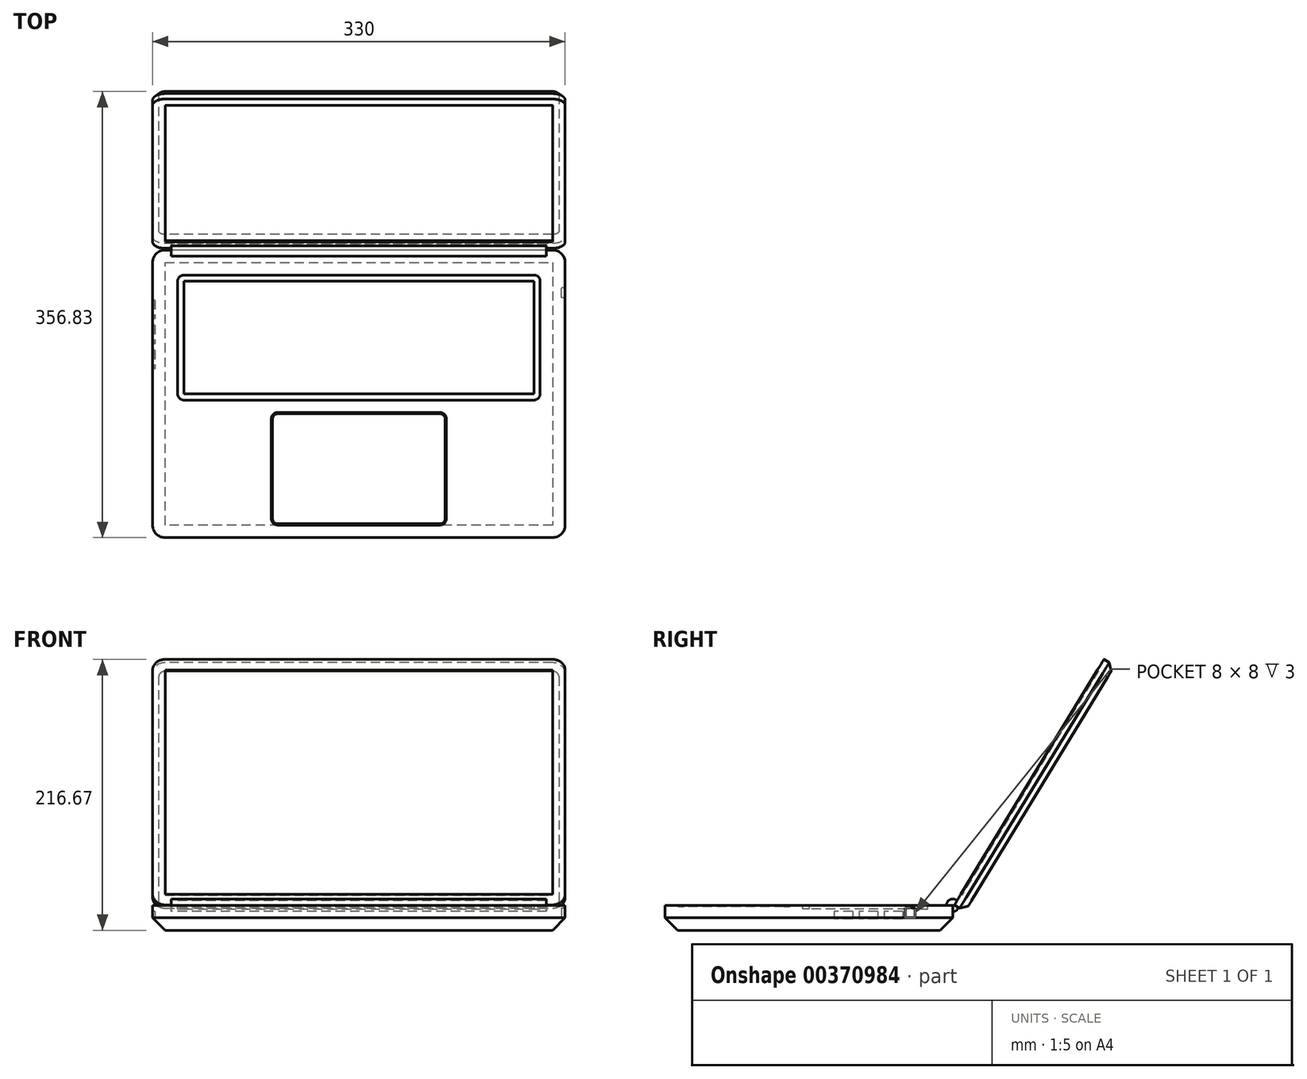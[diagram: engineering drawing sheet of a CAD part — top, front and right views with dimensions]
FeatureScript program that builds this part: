
annotation { "Feature Type Name" : "Feature", "Feature Type Description" : "" }
export const myFeature = defineFeature(function(context is Context, id is Id, definition is map)
    precondition{}
    {
        {
            var Q0;
            Q0=qCreatedBy(makeId("Right.planeOp"),FACE);
            var sketch = newSketch(context, id + "F0", { "sketchPlane" : qUnion([Q0])});
            skCircle(sketch, "E0", {"center": v(0, 0) * mm, "radius": 5 * mm});
            skSolve(sketch);
        }
        {
            var Q0;
            Q0=qCreatedBy(makeId("Right.planeOp"),FACE);
            var sketch = newSketch(context, id + "F1", { "sketchPlane" : qUnion([Q0])});
            skLineSegment(sketch, "E1.bottom", {"start": v(0, 0) * mm, "end": v(-230, 0) * mm});
            skLineSegment(sketch, "E1.top", {"start": v(0, -20) * mm, "end": v(-230, -20) * mm});
            skLineSegment(sketch, "E1.left", {"start": v(0, 0) * mm, "end": v(0, -20) * mm});
            skLineSegment(sketch, "E1.right", {"start": v(-230, 0) * mm, "end": v(-230, -20) * mm});
            skSolve(sketch);
        }
        {
            var Q0;
            Q0 = qSketchRegion(id + "F1", true);
            extrude(context, id + "F2", {"entities" : qUnion([Q0]), "endBound" : BoundingType.SYMMETRIC, "depth" : 330 * mm});
        }
        {
            var Q0;
            Q0 = qSketchRegion(id + "F0", true);
            extrude(context, id + "F3", {"entities" : qUnion([Q0]), "operationType" : NewBodyOperationType.ADD, "endBound" : BoundingType.SYMMETRIC, "depth" : 300 * mm});
        }
        {
            var Q0;
            Q0=makeQuery(id+"F2.opExtrude","CAP_EDGE",EDGE,{"disambiguationData":[OSD([sQuery(id+"F1.wireOp",EDGE,"V3VyQ788-CHpF-L9UI-HHIn-uLbdnDteFLPi")])],"isStart":false});
            var Q1;
            Q1=makeQuery(id+"F2.opExtrude","CAP_EDGE",EDGE,{"disambiguationData":[OSD([sQuery(id+"F1.wireOp",EDGE,"V3VyQ788-CHpF-L9UI-HHIn-uLbdnDteFLPi")])],"isStart":true});
            var Q2;
            Q2=makeQuery(id+"F2.opExtrude","CAP_EDGE",EDGE,{"disambiguationData":[OSD([sQuery(id+"F1.wireOp",EDGE,"1viRVT48-LFa6-ff3u-HfjB-U5OnZZm2wvsv")])],"isStart":false});
            var Q3;
            Q3=makeQuery(id+"F2.opExtrude","CAP_EDGE",EDGE,{"disambiguationData":[OSD([sQuery(id+"F1.wireOp",EDGE,"1viRVT48-LFa6-ff3u-HfjB-U5OnZZm2wvsv")])],"isStart":true});
            var Q4;
            Q4=makeQuery(id+"F2.opExtrude","CAP_EDGE",EDGE,{"disambiguationData":[OSD([sQuery(id+"F1.wireOp",EDGE,"E1.left")])],"isStart":true});
            var Q5;
            Q5=makeQuery(id+"F2.opExtrude","CAP_EDGE",EDGE,{"disambiguationData":[OSD([sQuery(id+"F1.wireOp",EDGE,"E1.right")])],"isStart":true});
            var Q6;
            Q6=makeQuery(id+"F2.opExtrude","CAP_EDGE",EDGE,{"disambiguationData":[OSD([sQuery(id+"F1.wireOp",EDGE,"E1.right")])],"isStart":false});
            var Q7;
            Q7=makeQuery(id+"F2.opExtrude","CAP_EDGE",EDGE,{"disambiguationData":[OSD([sQuery(id+"F1.wireOp",EDGE,"E1.left")])],"isStart":false});
            fillet(context, id + "F4", {"entities" : qUnion([Q0, Q1, Q2, Q3, Q4, Q5, Q6, Q7]), "radius" : 10 * mm, "tangentPropagation" : true, "allowEdgeOverflow" : false});
        }
        {
            var Q0;
            Q0=makeQuery(id+"F2.opExtrude","CAP_EDGE",EDGE,{"disambiguationData":[OSD([sQuery(id+"F1.wireOp",EDGE,"E1.top")])],"isStart":false});
            chamfer(context, id + "F5", {"entities" : qUnion([Q0]), "width" : 10 * mm, "tangentPropagation" : true});
        }
        {
            var Q0;
            Q0=makeQuery(id+"F2.opExtrude","SWEPT_FACE",FACE,{"disambiguationData":[OSD([sQuery(id+"F1.wireOp",EDGE,"E1.bottom")])]});
            var sketch = newSketch(context, id + "F6", { "sketchPlane" : qUnion([Q0])});
            skLineSegment(sketch, "E2.bottom", {"start": v(-140, -20) * mm, "end": v(140, -20) * mm});
            skLineSegment(sketch, "E2.top", {"start": v(-140, -120) * mm, "end": v(140, -120) * mm});
            skLineSegment(sketch, "E2.left", {"start": v(-145, -25) * mm, "end": v(-145, -115) * mm});
            skLineSegment(sketch, "E2.right", {"start": v(145, -25) * mm, "end": v(145, -115) * mm});
            skPoint(sketch, "E3.visualSharp", {"position": v(-145, -20) * mm});
            skArc(sketch, "E3.filletArc", {"start": v(-140, -20) * mm, "mid": v(-143.54, -21.46) * mm, "end": v(-145, -25) * mm});
            skPoint(sketch, "E4.visualSharp", {"position": v(-145, -120) * mm});
            skArc(sketch, "E4.filletArc", {"start": v(-145, -115) * mm, "mid": v(-143.54, -118.54) * mm, "end": v(-140, -120) * mm});
            skPoint(sketch, "E5.visualSharp", {"position": v(145, -120) * mm});
            skArc(sketch, "E5.filletArc", {"start": v(140, -120) * mm, "mid": v(143.54, -118.54) * mm, "end": v(145, -115) * mm});
            skPoint(sketch, "E6.visualSharp", {"position": v(145, -20) * mm});
            skArc(sketch, "E6.filletArc", {"start": v(145, -25) * mm, "mid": v(143.54, -21.46) * mm, "end": v(140, -20) * mm});
            skSolve(sketch);
        }
        {
            var Q0;
            Q0 = qSketchRegion(id + "F6", true);
            extrude(context, id + "F7", {"entities" : qUnion([Q0]), "operationType" : NewBodyOperationType.REMOVE, "oppositeDirection" : true, "depth" : 3 * mm});
        }
        {
            var Q0;
            Q0=makeQuery(id+"F7.boolean.opBoolean","COPY",FACE,{"derivedFrom":makeQuery(id+"F7.opExtrude","CAP_FACE",FACE,{"disambiguationData":[OSD([sQuery(id+"F6.wireOp",EDGE,"E2.bottom"),sQuery(id+"F6.wireOp",EDGE,"E2.top"),sQuery(id+"F6.wireOp",EDGE,"E2.left"),sQuery(id+"F6.wireOp",EDGE,"E2.right"),sQuery(id+"F6.wireOp",EDGE,"E3.filletArc"),sQuery(id+"F6.wireOp",EDGE,"E4.filletArc"),sQuery(id+"F6.wireOp",EDGE,"E5.filletArc"),sQuery(id+"F6.wireOp",EDGE,"E6.filletArc")])],"isStart":false})});
            var sketch = newSketch(context, id + "F8", { "sketchPlane" : qUnion([Q0])});
            skLineSegment(sketch, "E7.bottom", {"start": v(-140, -25) * mm, "end": v(140, -25) * mm});
            skLineSegment(sketch, "E7.top", {"start": v(-140, -115) * mm, "end": v(140, -115) * mm});
            skLineSegment(sketch, "E7.left", {"start": v(-140, -25) * mm, "end": v(-140, -115) * mm});
            skLineSegment(sketch, "E7.right", {"start": v(140, -25) * mm, "end": v(140, -115) * mm});
            skSolve(sketch);
        }
        {
            var Q0;
            Q0 = qSketchRegion(id + "F8", true);
            extrude(context, id + "F9", {"entities" : qUnion([Q0]), "operationType" : NewBodyOperationType.ADD, "depth" : 3 * mm});
        }
        {
            var Q0;
            Q0=makeQuery(id+"F2.opExtrude","SWEPT_FACE",FACE,{"disambiguationData":[OSD([sQuery(id+"F1.wireOp",EDGE,"E1.bottom")])]});
            var sketch = newSketch(context, id + "F10", { "sketchPlane" : qUnion([Q0])});
            skLineSegment(sketch, "E8.bottom", {"start": v(-65, -130) * mm, "end": v(65, -130) * mm});
            skLineSegment(sketch, "E8.top", {"start": v(-65, -220) * mm, "end": v(65, -220) * mm});
            skLineSegment(sketch, "E8.left", {"start": v(-70, -135) * mm, "end": v(-70, -215) * mm});
            skLineSegment(sketch, "E8.right", {"start": v(70, -135) * mm, "end": v(70, -215) * mm});
            skPoint(sketch, "E9.visualSharp", {"position": v(-70, -130) * mm});
            skArc(sketch, "E9.filletArc", {"start": v(-65, -130) * mm, "mid": v(-68.54, -131.46) * mm, "end": v(-70, -135) * mm});
            skPoint(sketch, "E10.visualSharp", {"position": v(-70, -220) * mm});
            skArc(sketch, "E10.filletArc", {"start": v(-70, -215) * mm, "mid": v(-68.54, -218.54) * mm, "end": v(-65, -220) * mm});
            skPoint(sketch, "E11.visualSharp", {"position": v(70, -220) * mm});
            skArc(sketch, "E11.filletArc", {"start": v(65, -220) * mm, "mid": v(68.54, -218.54) * mm, "end": v(70, -215) * mm});
            skPoint(sketch, "E12.visualSharp", {"position": v(70, -130) * mm});
            skArc(sketch, "E12.filletArc", {"start": v(70, -135) * mm, "mid": v(68.54, -131.46) * mm, "end": v(65, -130) * mm});
            skLineSegment(sketch, "E13.0", {"start": v(-65, -131) * mm, "end": v(65, -131) * mm});
            skArc(sketch, "E13.1", {"start": v(69, -135) * mm, "mid": v(67.83, -132.17) * mm, "end": v(65, -131) * mm});
            skArc(sketch, "E13.2", {"start": v(-65, -131) * mm, "mid": v(-67.83, -132.17) * mm, "end": v(-69, -135) * mm});
            skLineSegment(sketch, "E13.3", {"start": v(69, -135) * mm, "end": v(69, -215) * mm});
            skLineSegment(sketch, "E13.4", {"start": v(-69, -135) * mm, "end": v(-69, -215) * mm});
            skArc(sketch, "E13.5", {"start": v(-69, -215) * mm, "mid": v(-67.83, -217.83) * mm, "end": v(-65, -219) * mm});
            skLineSegment(sketch, "E13.6", {"start": v(-65, -219) * mm, "end": v(65, -219) * mm});
            skArc(sketch, "E13.7", {"start": v(65, -219) * mm, "mid": v(67.83, -217.83) * mm, "end": v(69, -215) * mm});
            skSolve(sketch);
        }
        {
            var Q0;
            Q0 = qSketchRegion(id + "F10", true);
            extrude(context, id + "F11", {"entities" : qUnion([Q0]), "operationType" : NewBodyOperationType.REMOVE, "oppositeDirection" : true, "depth" : 1 * mm});
        }
        {
            var Q0;
            Q0=qCreatedBy(makeId("Right.planeOp"),FACE);
            var sketch = newSketch(context, id + "F12", { "sketchPlane" : qUnion([Q0])});
            skLineSegment(sketch, "E14", {"start": v(1.37, 0.32) * mm, "end": v(9.84, -5) * mm});
            skLineSegment(sketch, "E15", {"start": v(9.84, -5) * mm, "end": v(129.43, 191.47) * mm});
            skLineSegment(sketch, "E16", {"start": v(129.43, 191.47) * mm, "end": v(120.9, 196.67) * mm});
            skLineSegment(sketch, "E17", {"start": v(120.9, 196.67) * mm, "end": v(1.37, 0.32) * mm});
            skSolve(sketch);
        }
        {
            var Q0;
            Q0 = qSketchRegion(id + "F12", true);
            extrude(context, id + "F13", {"entities" : qUnion([Q0]), "operationType" : NewBodyOperationType.ADD, "endBound" : BoundingType.SYMMETRIC, "depth" : 330 * mm});
        }
        {
            var Q0;
            Q0=makeQuery(id+"F13.opExtrude","CAP_EDGE",EDGE,{"disambiguationData":[OSD([sQuery(id+"F12.wireOp",EDGE,"E16")])],"isStart":true});
            var Q1;
            Q1=makeQuery(id+"F13.opExtrude","CAP_EDGE",EDGE,{"disambiguationData":[OSD([sQuery(id+"F12.wireOp",EDGE,"E16")])],"isStart":false});
            var Q2;
            Q2=makeQuery(id+"F13.opExtrude","CAP_EDGE",EDGE,{"disambiguationData":[OSD([sQuery(id+"F12.wireOp",EDGE,"E14")])],"isStart":false});
            var Q3;
            Q3=makeQuery(id+"F13.opExtrude","CAP_EDGE",EDGE,{"disambiguationData":[OSD([sQuery(id+"F12.wireOp",EDGE,"E14")])],"isStart":true});
            fillet(context, id + "F14", {"entities" : qUnion([Q0, Q1, Q2, Q3]), "radius" : 10 * mm, "tangentPropagation" : true, "allowEdgeOverflow" : false});
        }
        {
            var Q0;
            Q0=makeQuery(id+"F13.opExtrude","CAP_EDGE",EDGE,{"disambiguationData":[OSD([sQuery(id+"F12.wireOp",EDGE,"E15")])],"isStart":false});
            chamfer(context, id + "F15", {"entities" : qUnion([Q0]), "width" : 5 * mm, "tangentPropagation" : true});
        }
        {
            var Q0;
            Q0=makeQuery(id+"F13.opExtrude","SWEPT_FACE",FACE,{"disambiguationData":[OSD([sQuery(id+"F12.wireOp",EDGE,"E17")])]});
            var sketch = newSketch(context, id + "F16", { "sketchPlane" : qUnion([Q0])});
            skLineSegment(sketch, "E18.bottom", {"start": v(-155, 220.85) * mm, "end": v(155, 220.85) * mm});
            skLineSegment(sketch, "E18.top", {"start": v(-155, 10.92) * mm, "end": v(155, 10.92) * mm});
            skLineSegment(sketch, "E18.left", {"start": v(-155, 220.85) * mm, "end": v(-155, 10.92) * mm});
            skLineSegment(sketch, "E18.right", {"start": v(155, 220.85) * mm, "end": v(155, 10.92) * mm});
            skSolve(sketch);
        }
        {
            var Q0;
            Q0 = qSketchRegion(id + "F16", true);
            extrude(context, id + "F17", {"entities" : qUnion([Q0]), "operationType" : NewBodyOperationType.REMOVE, "oppositeDirection" : true, "depth" : 1 * mm});
        }
        {
            var Q0;
            Q0=makeQuery(id+"F2.opExtrude","CAP_FACE",FACE,{"disambiguationData":[OSD([sQuery(id+"F1.wireOp",EDGE,"E1.bottom"),sQuery(id+"F1.wireOp",EDGE,"E1.top"),sQuery(id+"F1.wireOp",EDGE,"E1.left"),sQuery(id+"F1.wireOp",EDGE,"E1.right")])],"isStart":true});
            var sketch = newSketch(context, id + "F18", { "sketchPlane" : qUnion([Q0])});
            skLineSegment(sketch, "E19.bottom", {"start": v(80, -5) * mm, "end": v(95, -5) * mm});
            skLineSegment(sketch, "E19.top", {"start": v(80, -11) * mm, "end": v(95, -11) * mm});
            skLineSegment(sketch, "E19.left", {"start": v(80, -5) * mm, "end": v(80, -11) * mm});
            skLineSegment(sketch, "E19.right", {"start": v(95, -5) * mm, "end": v(95, -11) * mm});
            skLineSegment(sketch, "E20.1.0.0", {"start": v(60, -5) * mm, "end": v(60, -11) * mm});
            skLineSegment(sketch, "E20.1.0.1", {"start": v(60, -5) * mm, "end": v(75, -5) * mm});
            skLineSegment(sketch, "E20.1.0.2", {"start": v(75, -5) * mm, "end": v(75, -11) * mm});
            skLineSegment(sketch, "E20.1.0.3", {"start": v(60, -11) * mm, "end": v(75, -11) * mm});
            skLineSegment(sketch, "E20.2.0.0", {"start": v(40, -5) * mm, "end": v(40, -11) * mm});
            skLineSegment(sketch, "E20.2.0.1", {"start": v(40, -5) * mm, "end": v(55, -5) * mm});
            skLineSegment(sketch, "E20.2.0.2", {"start": v(55, -5) * mm, "end": v(55, -11) * mm});
            skLineSegment(sketch, "E20.2.0.3", {"start": v(40, -11) * mm, "end": v(55, -11) * mm});
            skLineSegment(sketch, "E20.direction1", {"start": v(80, -11) * mm, "end": v(60, -11) * mm, "construction": true});
            skSolve(sketch);
        }
        {
            var Q0;
            Q0 = qSketchRegion(id + "F18", true);
            extrude(context, id + "F19", {"entities" : qUnion([Q0]), "operationType" : NewBodyOperationType.REMOVE, "oppositeDirection" : true, "depth" : 2 * mm});
        }
        {
            var Q0;
            Q0=makeQuery(id+"F2.opExtrude","CAP_FACE",FACE,{"disambiguationData":[OSD([sQuery(id+"F1.wireOp",EDGE,"E1.bottom"),sQuery(id+"F1.wireOp",EDGE,"E1.top"),sQuery(id+"F1.wireOp",EDGE,"E1.left"),sQuery(id+"F1.wireOp",EDGE,"E1.right")])],"isStart":false});
            var sketch = newSketch(context, id + "F20", { "sketchPlane" : qUnion([Q0])});
            skLineSegment(sketch, "E21.bottom", {"start": v(-38, -2) * mm, "end": v(-30, -2) * mm});
            skLineSegment(sketch, "E21.top", {"start": v(-38, -10) * mm, "end": v(-30, -10) * mm});
            skLineSegment(sketch, "E21.left", {"start": v(-38, -2) * mm, "end": v(-38, -10) * mm});
            skLineSegment(sketch, "E21.right", {"start": v(-30, -2) * mm, "end": v(-30, -10) * mm});
            skSolve(sketch);
        }
        {
            var Q0;
            Q0 = qSketchRegion(id + "F20", true);
            extrude(context, id + "F21", {"entities" : qUnion([Q0]), "operationType" : NewBodyOperationType.REMOVE, "oppositeDirection" : true, "depth" : 3 * mm});
        }
    });
